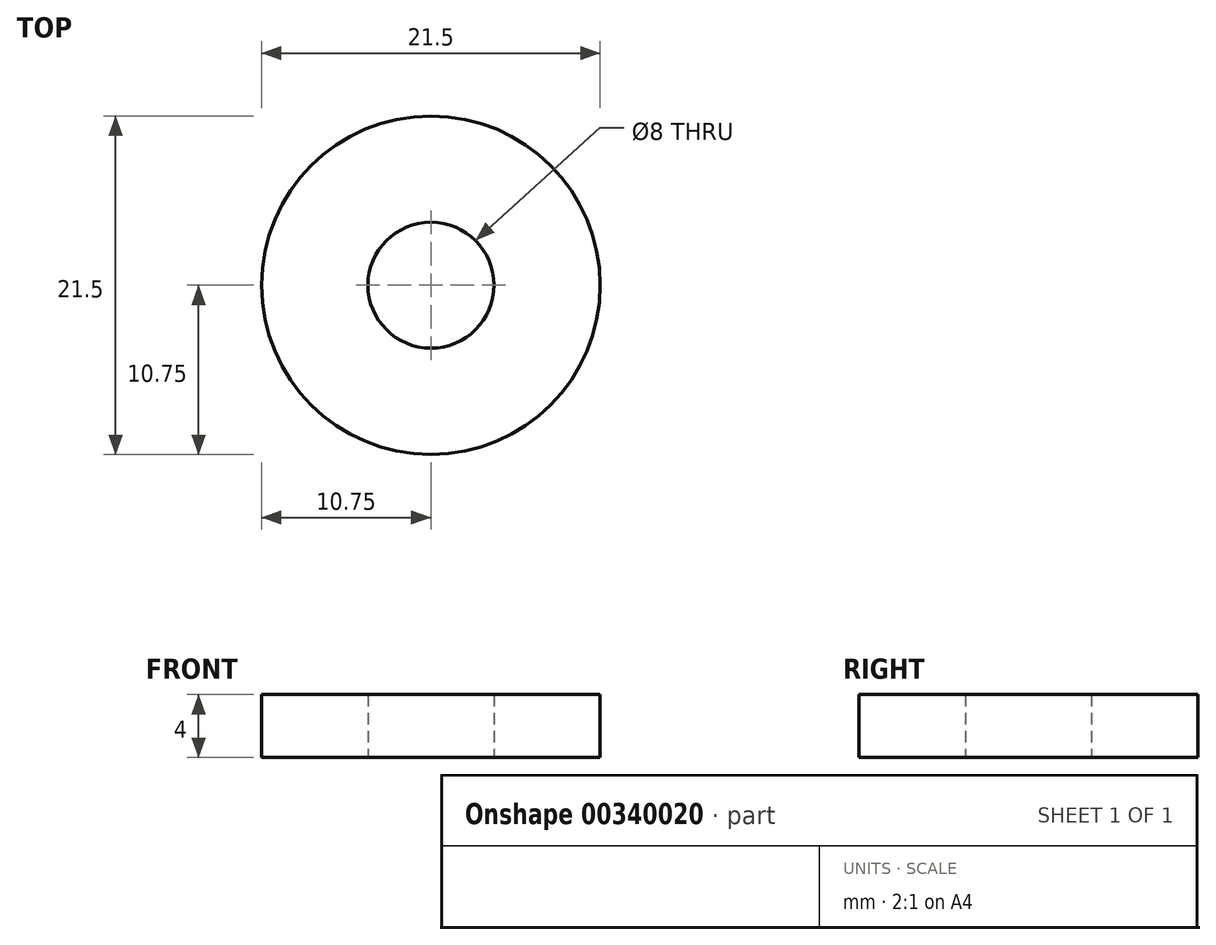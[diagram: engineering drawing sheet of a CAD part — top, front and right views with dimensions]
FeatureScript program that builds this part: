
annotation { "Feature Type Name" : "Feature", "Feature Type Description" : "" }
export const myFeature = defineFeature(function(context is Context, id is Id, definition is map)
    precondition{}
    {
        {
            var Q0;
            Q0=qCreatedBy(makeId("Top.planeOp"),FACE);
            var sketch = newSketch(context, id + "F0", { "sketchPlane" : qUnion([Q0])});
            skCircle(sketch, "E0", {"center": v(0, 0) * mm, "radius": 10.75 * mm});
            skCircle(sketch, "E1", {"center": v(0, 0) * mm, "radius": 4 * mm});
            skSolve(sketch);
        }
        {
            var Q0;
            Q0 = qSketchRegion(id + "F0", true);
            extrude(context, id + "F1", {"entities" : qUnion([Q0]), "depth" : 4 * mm});
        }
    });
